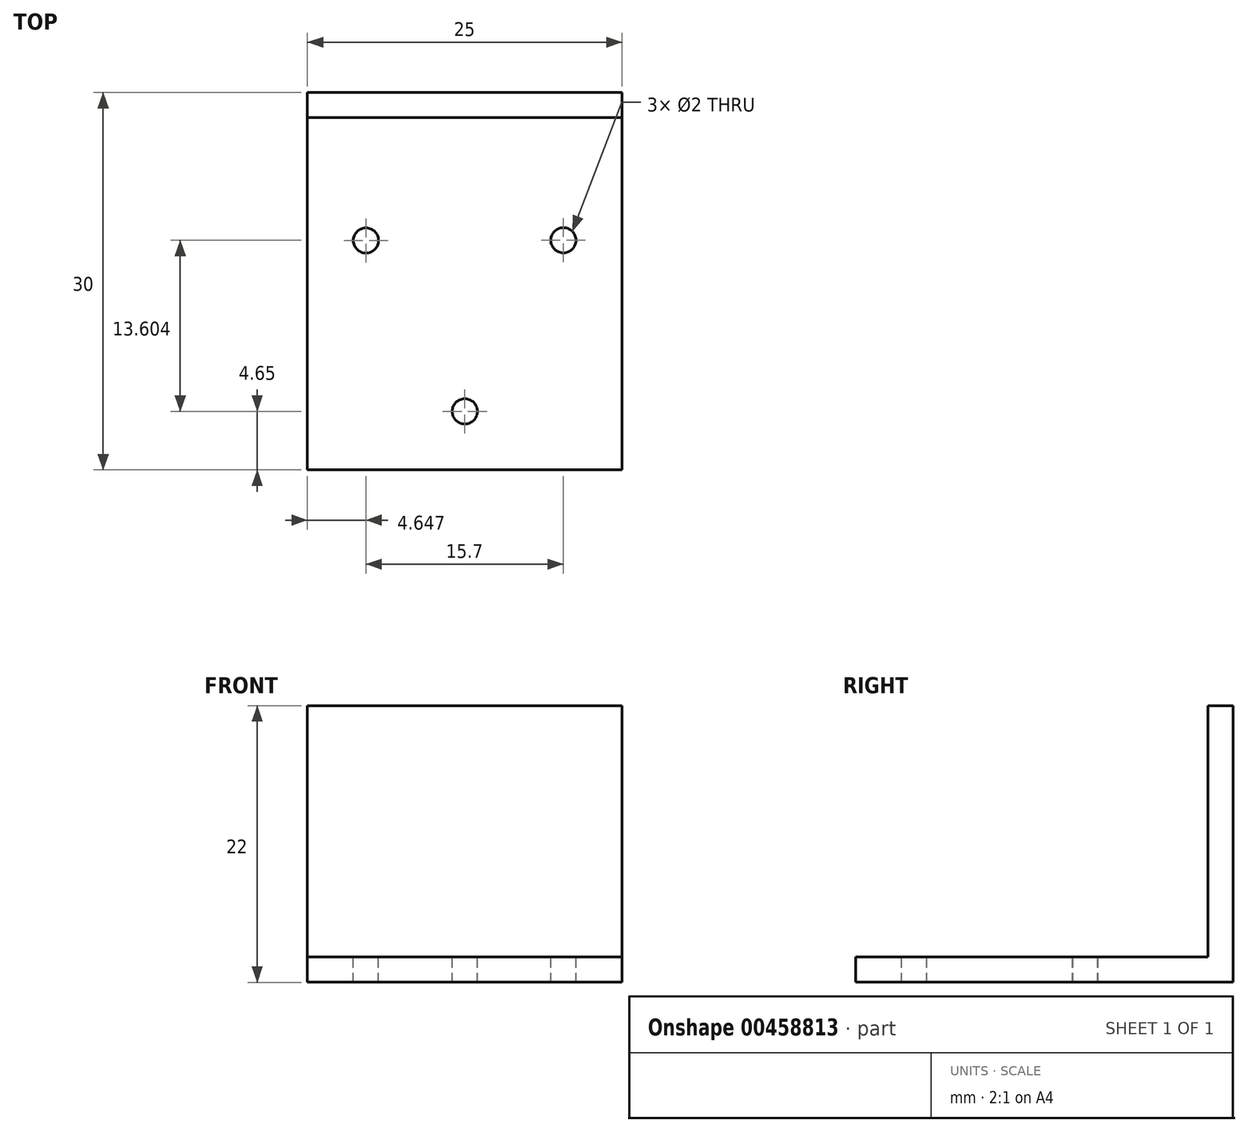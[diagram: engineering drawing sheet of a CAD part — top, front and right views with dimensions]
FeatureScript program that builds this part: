
annotation { "Feature Type Name" : "Feature", "Feature Type Description" : "" }
export const myFeature = defineFeature(function(context is Context, id is Id, definition is map)
    precondition{}
    {
        {
            var Q0;
            Q0=qCreatedBy(makeId("Front.planeOp"),FACE);
            var sketch = newSketch(context, id + "F0", { "sketchPlane" : qUnion([Q0])});
            skLineSegment(sketch, "E0", {"start": v(-14.45, -33.4) * mm, "end": v(10.55, -33.4) * mm});
            skLineSegment(sketch, "E1", {"start": v(-14.45, -33.4) * mm, "end": v(-14.45, -31.4) * mm});
            skLineSegment(sketch, "E2", {"start": v(10.55, -31.4) * mm, "end": v(10.55, -33.4) * mm});
            skLineSegment(sketch, "E3", {"start": v(-14.45, -31.4) * mm, "end": v(10.55, -31.4) * mm});
            skSolve(sketch);
        }
        {
            var Q0;
            Q0=makeQuery(id+"F0.imprint","IMPRINT",FACE,{"disambiguationData":[TD([[makeQuery(id+"F0.imprint","IMPRINT",EDGE,{"derivedFrom":sQuery(id+"F0.wireOp",EDGE,"E0")}),1.0]])]});
            extrude(context, id + "F1", {"entities" : qUnion([Q0]), "depth" : 25 * mm, "offsetDistance" : 25 * mm});
        }
        {
            var Q0;
            Q0=makeQuery(id+"F1.opExtrude","SWEPT_FACE",FACE,{"disambiguationData":[OSD([sQuery(id+"F0.wireOp",EDGE,"E3")])]});
            var sketch = newSketch(context, id + "F2", { "sketchPlane" : qUnion([Q0])});
            skCircle(sketch, "E4", {"center": v(-1.94, -20.35) * mm, "radius": 1 * mm});
            skCircle(sketch, "E5", {"center": v(5.9, -6.75) * mm, "radius": 1 * mm});
            skCircle(sketch, "E6", {"center": v(-9.8, -6.76) * mm, "radius": 1 * mm});
            skSolve(sketch);
        }
        {
            var Q0;
            Q0 = qSketchRegion(id + "F2", true);
            extrude(context, id + "F3", {"entities" : qUnion([Q0]), "operationType" : NewBodyOperationType.REMOVE, "oppositeDirection" : true, "depth" : 25 * mm, "offsetDistance" : 25 * mm});
        }
        {
            var Q0;
            Q0=makeQuery(id+"F1.opExtrude","CAP_FACE",FACE,{"disambiguationData":[OSD([sQuery(id+"F0.wireOp",EDGE,"E0"),sQuery(id+"F0.wireOp",EDGE,"E1"),sQuery(id+"F0.wireOp",EDGE,"E2"),sQuery(id+"F0.wireOp",EDGE,"E3")])],"isStart":true});
            extrude(context, id + "F4", {"entities" : qUnion([Q0]), "operationType" : NewBodyOperationType.ADD, "depth" : 5 * mm, "offsetDistance" : 25 * mm});
        }
        {
            var Q0;
            {var subQ0=sQuery(id+"F0.wireOp",EDGE,"E3");Q0=makeQuery(id+"F4.boolean.opBoolean","MERGE",FACE,{"derivedFrom":[makeQuery(id+"F1.opExtrude","SWEPT_FACE",FACE,{"disambiguationData":[OSD([subQ0])]}),makeQuery(id+"F4.opExtrude","SWEPT_FACE",FACE,{"disambiguationData":[OSD([subQ0])]})]});}
            var sketch = newSketch(context, id + "F5", { "sketchPlane" : qUnion([Q0])});
            skLineSegment(sketch, "E7", {"start": v(-14.45, 3) * mm, "end": v(10.43, 3) * mm});
            skLineSegment(sketch, "E8.bottom", {"start": v(-14.45, 3) * mm, "end": v(10.55, 3) * mm});
            skLineSegment(sketch, "E8.top", {"start": v(-14.45, 5) * mm, "end": v(10.55, 5) * mm});
            skLineSegment(sketch, "E8.left", {"start": v(-14.45, 3) * mm, "end": v(-14.45, 5) * mm});
            skLineSegment(sketch, "E8.right", {"start": v(10.55, 3) * mm, "end": v(10.55, 5) * mm});
            skSolve(sketch);
        }
        {
            var Q0;
            Q0 = qSketchRegion(id + "F5", true);
            extrude(context, id + "F6", {"entities" : qUnion([Q0]), "operationType" : NewBodyOperationType.ADD, "depth" : 20 * mm, "offsetDistance" : 25 * mm});
        }
    });
